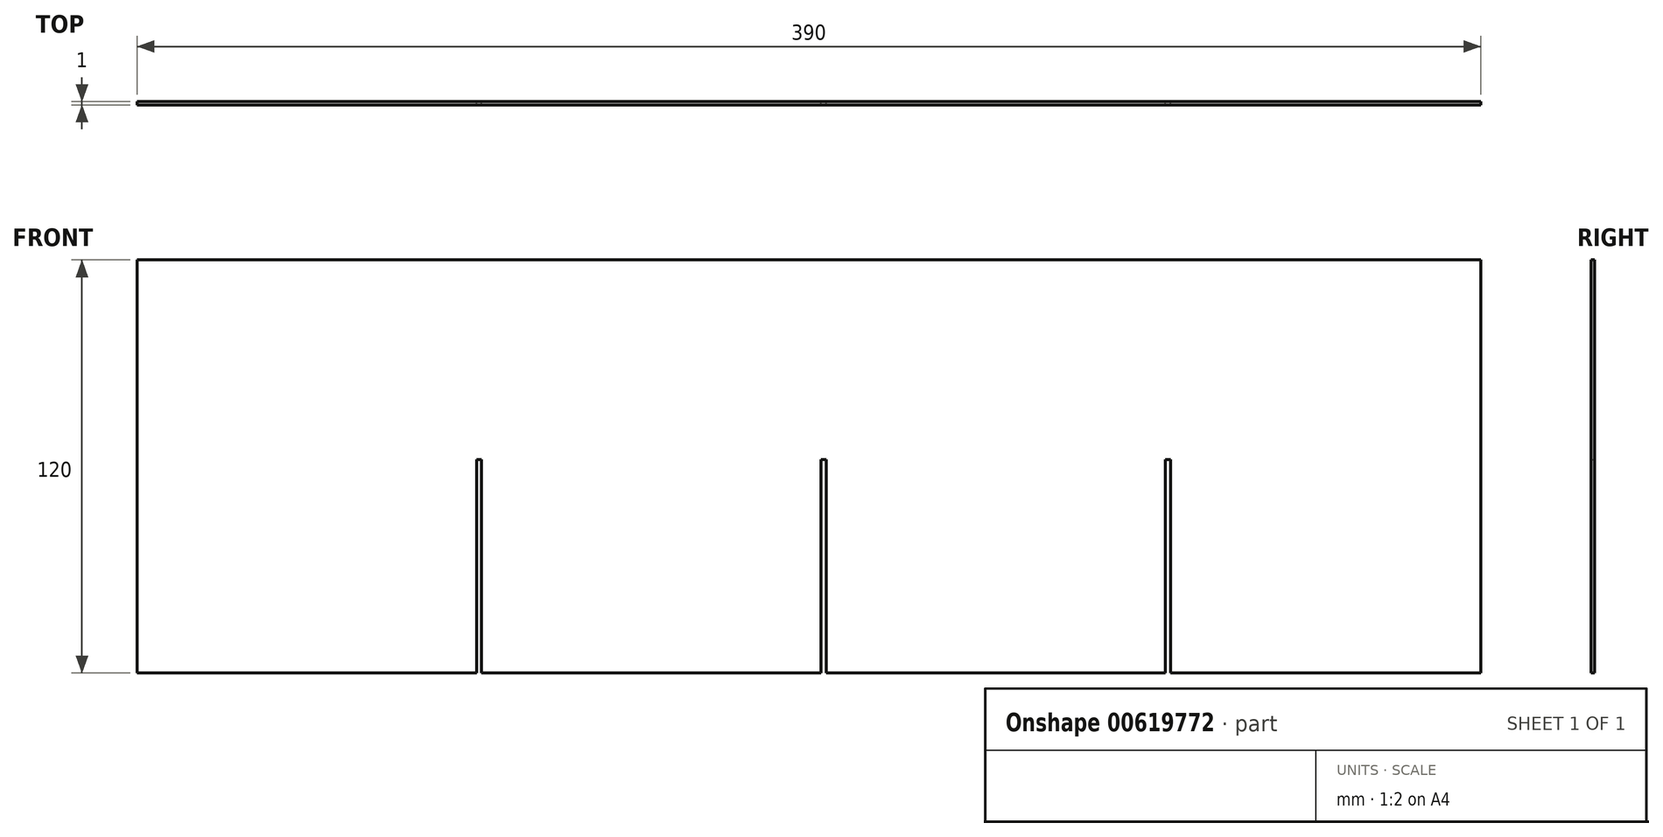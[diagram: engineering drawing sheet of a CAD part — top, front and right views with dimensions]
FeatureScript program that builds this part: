
annotation { "Feature Type Name" : "Feature", "Feature Type Description" : "" }
export const myFeature = defineFeature(function(context is Context, id is Id, definition is map)
    precondition{}
    {
        {
            var Q0;
            Q0=qCreatedBy(makeId("Front.planeOp"),FACE);
            var sketch = newSketch(context, id + "F0", { "sketchPlane" : qUnion([Q0])});
            skLineSegment(sketch, "E0", {"start": v(-67.02, -9.71) * mm, "end": v(31.48, -9.71) * mm});
            skLineSegment(sketch, "E1", {"start": v(31.48, -9.71) * mm, "end": v(31.48, 52.29) * mm});
            skLineSegment(sketch, "E2", {"start": v(31.48, 52.29) * mm, "end": v(32.98, 52.29) * mm});
            skLineSegment(sketch, "E3", {"start": v(32.98, 52.29) * mm, "end": v(32.98, -9.71) * mm});
            skLineSegment(sketch, "E4", {"start": v(32.98, -9.71) * mm, "end": v(131.48, -9.71) * mm});
            skLineSegment(sketch, "E5", {"start": v(131.48, -9.71) * mm, "end": v(131.48, 52.29) * mm});
            skLineSegment(sketch, "E6", {"start": v(131.48, 52.29) * mm, "end": v(132.98, 52.29) * mm});
            skLineSegment(sketch, "E7", {"start": v(132.98, 52.29) * mm, "end": v(132.98, -9.71) * mm});
            skLineSegment(sketch, "E8", {"start": v(132.98, -9.71) * mm, "end": v(231.48, -9.71) * mm});
            skLineSegment(sketch, "E9", {"start": v(231.48, -9.71) * mm, "end": v(231.48, 52.29) * mm});
            skLineSegment(sketch, "E10", {"start": v(231.48, 52.29) * mm, "end": v(232.98, 52.29) * mm});
            skLineSegment(sketch, "E11", {"start": v(232.98, 52.29) * mm, "end": v(232.98, -9.71) * mm});
            skLineSegment(sketch, "E12", {"start": v(-67.02, -9.71) * mm, "end": v(-67.02, 110.29) * mm});
            skLineSegment(sketch, "E13", {"start": v(-67.02, 110.29) * mm, "end": v(322.98, 110.29) * mm});
            skLineSegment(sketch, "E14", {"start": v(232.98, -9.71) * mm, "end": v(322.98, -9.71) * mm});
            skLineSegment(sketch, "E15", {"start": v(322.98, 110.29) * mm, "end": v(322.98, -9.71) * mm});
            skSolve(sketch);
        }
        {
            var Q0;
            Q0=makeQuery(id+"F0.imprint","IMPRINT",FACE,{"disambiguationData":[TD([[makeQuery(id+"F0.imprint","IMPRINT",EDGE,{"derivedFrom":sQuery(id+"F0.wireOp",EDGE,"E0")}),1.0]])]});
            extrude(context, id + "F1", {"entities" : qUnion([Q0]), "depth" : 1 * mm, "offsetDistance" : 25 * mm});
        }
    });
